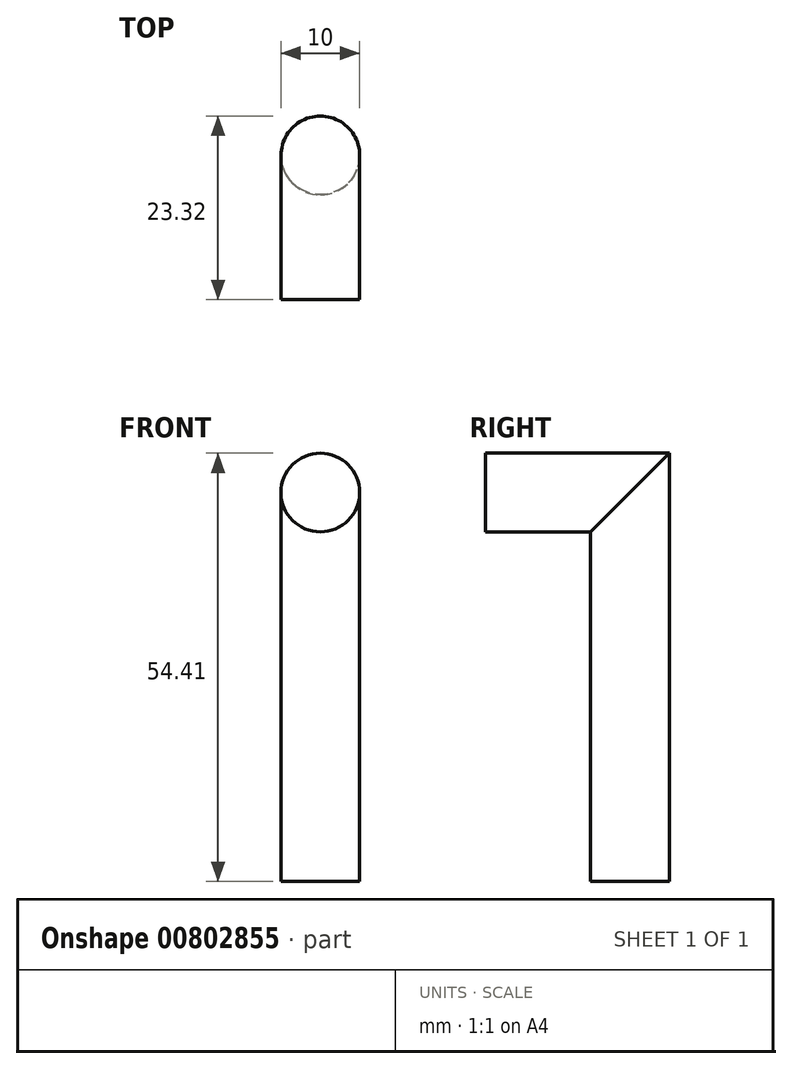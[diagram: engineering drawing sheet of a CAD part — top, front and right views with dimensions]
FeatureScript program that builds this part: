
annotation { "Feature Type Name" : "Feature", "Feature Type Description" : "" }
export const myFeature = defineFeature(function(context is Context, id is Id, definition is map)
    precondition{}
    {
        {
            var Q0;
            Q0=qCreatedBy(makeId("Front.planeOp"),FACE);
            var sketch = newSketch(context, id + "F0", { "sketchPlane" : qUnion([Q0])});
            skCircle(sketch, "E0", {"center": v(0, 32.99) * mm, "radius": 5 * mm});
            skSolve(sketch);
        }
        {
            var Q0;
            Q0=qCreatedBy(makeId("Right.planeOp"),FACE);
            var sketch = newSketch(context, id + "F1", { "sketchPlane" : qUnion([Q0])});
            skLineSegment(sketch, "E1", {"start": v(18.92, 33.58) * mm, "end": v(0, 33.58) * mm});
            skLineSegment(sketch, "E2", {"start": v(18.92, 33.58) * mm, "end": v(18.92, -16.42) * mm});
            skSolve(sketch);
        }
        {
            var Q0;
            Q0=makeQuery(id+"F0.imprint","IMPRINT",FACE,{"disambiguationData":[TD([[makeQuery(id+"F0.imprint","IMPRINT",EDGE,{"derivedFrom":sQuery(id+"F0.wireOp",EDGE,"E0")}),1.0]])]});
            var Q1;
            Q1=sQuery(id+"F1.wireOp",EDGE,"E1");
            var Q2;
            Q2=sQuery(id+"F1.wireOp",EDGE,"E2");
            sweep(context, id + "F2", {"profiles" : qUnion([Q0]), "path" : qUnion([Q1, Q2])});
        }
    });
